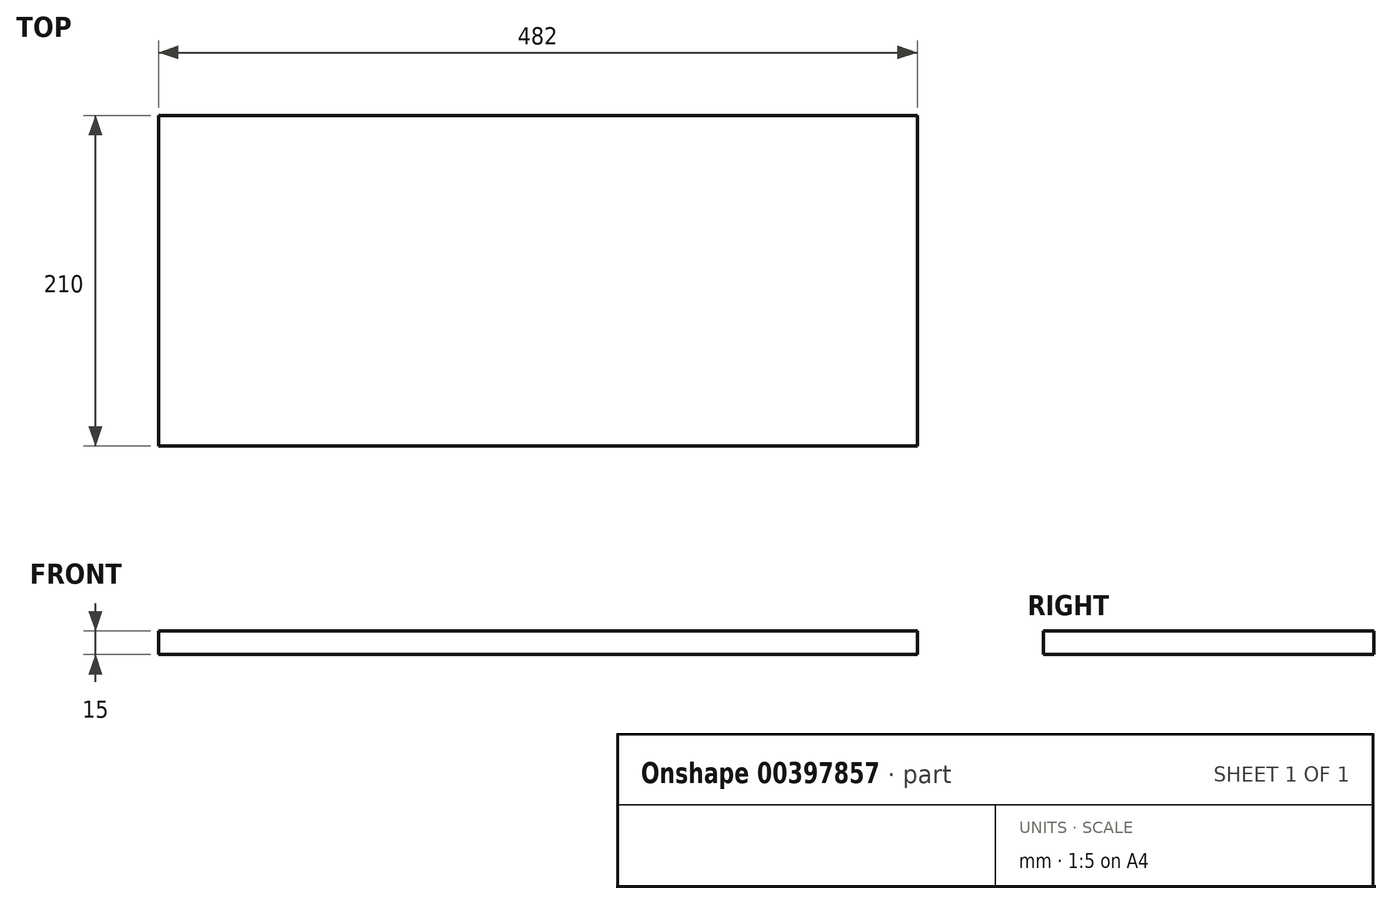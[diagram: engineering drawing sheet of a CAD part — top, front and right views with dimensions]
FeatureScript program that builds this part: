
annotation { "Feature Type Name" : "Feature", "Feature Type Description" : "" }
export const myFeature = defineFeature(function(context is Context, id is Id, definition is map)
    precondition{}
    {
        {
            var Q0;
            Q0=qCreatedBy(makeId("Top.planeOp"),FACE);
            var sketch = newSketch(context, id + "F0", { "sketchPlane" : qUnion([Q0])});
            skLineSegment(sketch, "E0.bottom", {"start": v(241, -105) * mm, "end": v(-241, -105) * mm});
            skLineSegment(sketch, "E0.top", {"start": v(241, 105) * mm, "end": v(-241, 105) * mm});
            skLineSegment(sketch, "E0.left", {"start": v(241, -105) * mm, "end": v(241, 105) * mm});
            skLineSegment(sketch, "E0.right", {"start": v(-241, -105) * mm, "end": v(-241, 105) * mm});
            skPoint(sketch, "E0.middle", {"position": v(0, 0) * mm});
            skSolve(sketch);
        }
        {
            var Q0;
            Q0=makeQuery(id+"F0.imprint","IMPRINT",FACE,{"disambiguationData":[TD([[makeQuery(id+"F0.imprint","IMPRINT",EDGE,{"derivedFrom":sQuery(id+"F0.wireOp",EDGE,"E0.bottom")}),-1.0]])]});
            extrude(context, id + "F1", {"entities" : qUnion([Q0]), "oppositeDirection" : true, "depth" : 15 * mm});
        }
    });
